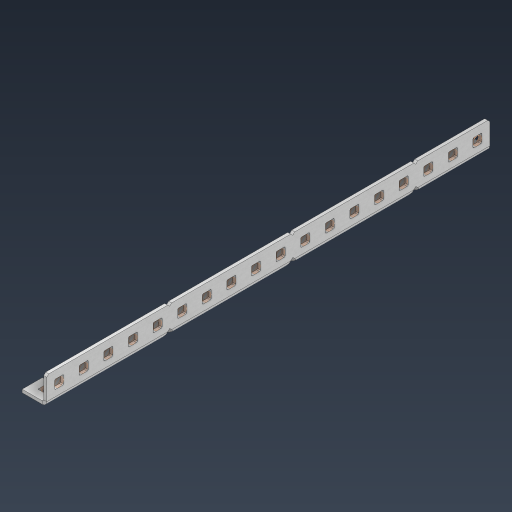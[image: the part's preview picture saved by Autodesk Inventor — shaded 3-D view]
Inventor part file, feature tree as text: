
AUTODESK INVENTOR PART (.ipt)
format: ipt  version: 2024.3 (Build 283343000, 343)  size: 810,496 bytes
history: native  units: in
note: dims shown in document units (in); Inventor stores cm internally (conversion verified against a paired STEP export)
features: other x61, extrude x52, sheet_metal_op x11, pattern_linear x2, mirror x1, chamfer x1, sketch x1
ambient origin geometry x8: Origin, YZ Plane, XZ Plane, XY Plane, X Axis, Y Axis, Z Axis, Center Point
bodies: Solid1 (feature_tree), Body (feature_tree)
feature tree (129):
  sheet_metal_op  "Flanges"
  other  "Flange Pattern Plane"
  other  "Flange Pattern Sketch"
  sheet_metal_op  "Flange Pattern"
  sheet_metal_op  "Body Pattern"
  pattern_linear  "Center Pattern"  Spacing1=9.0in  [1 undecoded]
  other  "Arc Length"
  mirror  "Notch Mirror"
  pattern_linear  "Notch Pattern"  Spacing1=0.0625in  [1 undecoded]
  chamfer  "End Chamfer"
  extrude  "Half Cut"  Depth=0.0625in
  other  "Plate1"
  sketch  "Sketch2"  dims[d0=1.0in d1=9.0in d2=0.0625in d3=0.0625in d4=0.0312in d5=0.125in d6=0.0625in d7=0.5in d8=90.0deg d9=0.0312in d10=0.25in d11=0.0625in d12=0.0625in d16=0.182in d17=0.02in d18=0.0625in d19=0.0in d20=0.25in d21=0.25in d38=7.0866in d40=0.5in d41=0.3937in d43=1.0in d46=0.172in d47=1.0in d48=0.0in d49=0.182in d50=0.02in d51=0.25in d52=0.25in d53=0.0625in d54=0.0in d55=0.172in d56=1.0in d57=0.0in d58=0.25in d60=7.0866in d62=0.5in d63=0.3937in d65=0.5in d85=0.1473in d86=0.1782in d88=0.04in d89=0.0625in d90=0.0in d91=0.04in d92=0.0491in d95=2.5in d96=0.04in d97=0.25in d98=45.0deg d99=0.25in d100=0.5in d101=0.0in d102=2.497in d106=0.182in d107=0.02in d108=0.5in d109=0.5in d110=0.0625in d111=0.0in d112=0.172in d113=0.5in d114=0.0in d117=0.5in d118=0.5in d119=0.5in]
  other  "Plate2"
  sheet_metal_op  "Bend1"
  sheet_metal_op  "Corner1"
  other  "Srf1"
  other  "Srf2"
  other  "Srf91"
  sheet_metal_op  "Body Pattern Sketch"
  other  "Srf92"
  other  "Srf786"
  other  "Srf823"
  other  "Srf824"
  other  "Srf825"
  other  "Srf826"
  other  "Srf827"
  other  "Srf828"
  other  "Srf829"
  other  "Srf856"
  other  "Srf857"
  other  "Srf858"
  other  "Srf859"
  other  "Srf860"
  other  "Srf861"
  other  "Srf862"
  other  "Srf889"
  other  "Srf890"
  other  "Srf891"
  other  "Srf892"
  other  "Srf893"
  other  "Srf894"
  other  "Srf895"
  other  "Srf896"
  other  "Srf922"
  other  "Srf923"
  other  "Srf924"
  other  "Srf925"
  other  "Srf926"
  other  "Srf959"
  other  "Srf960"
  other  "Srf961"
  other  "Srf962"
  other  "Srf963"
  other  "Srf996"
  other  "Srf997"
  other  "Srf998"
  other  "Srf999"
  other  "Srf1000"
  other  "Srf1143"
  other  "Srf1144"
  other  "Srf1145"
  other  "Srf1146"
  other  "Srf1199"
  other  "Srf1200"
  other  "Srf1201"
  other  "Srf1202"
  other  "Srf1255"
  other  "Srf1256"
  other  "Srf1257"
  other  "Srf1258"
  sheet_metal_op  "Flange Stamp"
  sheet_metal_op  "Flange Circle"
  sheet_metal_op  "Body Stamp"
  sheet_metal_op  "Body Circle"
  other  "Center Stamp"
  other  "Center Circle"
  sheet_metal_op  "Notch"
  extrude  "ExtrusionSrf2"  Depth=0.0312in
  extrude  "ExtrusionSrf92"  Depth=0.5in
  extrude  "ExtrusionSrf823"  Depth=0.0625in
  extrude  "ExtrusionSrf824"  Depth=0.5in TaperAngle=90.0deg
  extrude  "ExtrusionSrf825"  Depth=0.25in
  extrude  "ExtrusionSrf826"  Depth=0.0625in
  extrude  "ExtrusionSrf827"  Depth=0.0625in
  extrude  "ExtrusionSrf828"  Depth=0.182in
  extrude  "ExtrusionSrf829"  Depth=0.02in
  extrude  "ExtrusionSrf856"  Depth=0.0625in
  extrude  "ExtrusionSrf857"  TaperAngle=0.0deg  [1 undecoded]
  extrude  "ExtrusionSrf858"  Depth=0.25in
  extrude  "ExtrusionSrf859"  Depth=0.25in
  extrude  "ExtrusionSrf860"  Depth=0.5in
  extrude  "ExtrusionSrf861"  Depth=0.5in
  extrude  "ExtrusionSrf862"  Depth=1.0in TaperAngle=0.0deg
  extrude  "ExtrusionSrf889"  Depth=0.182in
  extrude  "ExtrusionSrf890"  Depth=0.02in
  extrude  "ExtrusionSrf891"  Depth=0.25in
  extrude  "ExtrusionSrf892"  Depth=0.25in
  extrude  "ExtrusionSrf893"  Depth=0.0625in
  extrude  "ExtrusionSrf894"  TaperAngle=0.0deg  [1 undecoded]
  extrude  "ExtrusionSrf895"  Depth=0.5in
  extrude  "ExtrusionSrf896"  Depth=1.0in TaperAngle=0.0deg
  extrude  "ExtrusionSrf922"  Depth=0.25in
  extrude  "ExtrusionSrf923"  Depth=0.5in
  extrude  "ExtrusionSrf924"  Depth=0.5in
  extrude  "ExtrusionSrf925"  Depth=0.5in
  extrude  "ExtrusionSrf926"  Depth=0.5in
  extrude  "ExtrusionSrf959"  Depth=0.5in
  extrude  "ExtrusionSrf960"  Depth=0.0625in
  extrude  "ExtrusionSrf961"  TaperAngle=0.0deg  [1 undecoded]
  extrude  "ExtrusionSrf962"  Depth=0.5in
  extrude  "ExtrusionSrf963"  Depth=0.5in
  extrude  "ExtrusionSrf996"  Depth=2.5in
  extrude  "ExtrusionSrf997"  Depth=0.25in TaperAngle=45.0deg
  extrude  "ExtrusionSrf998"  Depth=0.25in
  extrude  "ExtrusionSrf999"  Depth=0.5in TaperAngle=0.0deg
  extrude  "ExtrusionSrf1000"  Depth=0.5in
  extrude  "ExtrusionSrf1143"  Depth=0.182in
  extrude  "ExtrusionSrf1144"  Depth=0.02in
  extrude  "ExtrusionSrf1145"  Depth=0.5in
  extrude  "ExtrusionSrf1146"  Depth=0.5in
  extrude  "ExtrusionSrf1199"  Depth=0.0625in
  extrude  "ExtrusionSrf1200"  TaperAngle=0.0deg  [1 undecoded]
  extrude  "ExtrusionSrf1201"  Depth=0.5in
  extrude  "ExtrusionSrf1202"  Depth=0.5in TaperAngle=0.0deg
  extrude  "ExtrusionSrf1255"  Depth=0.5in
  extrude  "ExtrusionSrf1256"  Depth=0.5in
  extrude  "ExtrusionSrf1257"  Depth=0.5in
  extrude  "ExtrusionSrf1258"  [1 undecoded]
note: 7 required parameter values undecoded (feature->parameter linkage not recoverable at this tier; creation-order binding heuristic only, values carry confidence <= 0.55)
